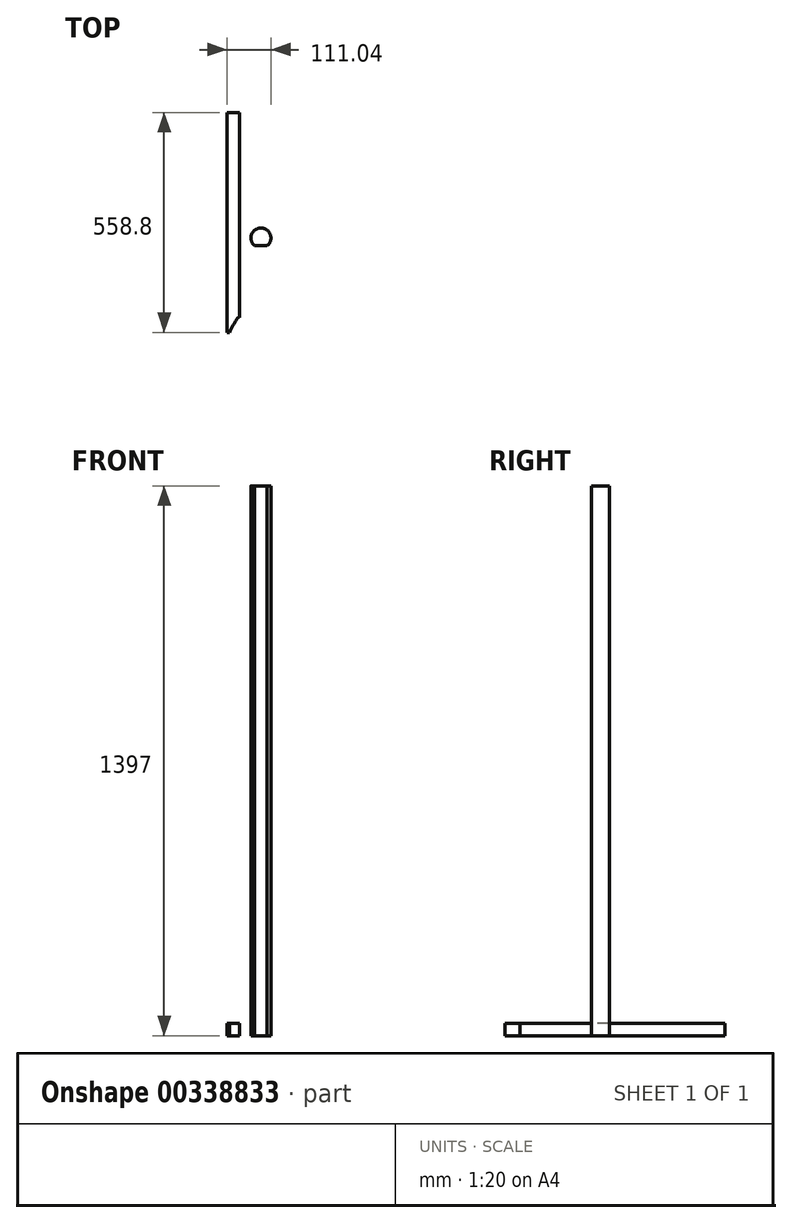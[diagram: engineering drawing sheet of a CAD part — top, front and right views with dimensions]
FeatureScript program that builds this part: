
annotation { "Feature Type Name" : "Feature", "Feature Type Description" : "" }
export const myFeature = defineFeature(function(context is Context, id is Id, definition is map)
    precondition{}
    {
        {
            var Q0;
            Q0=qCreatedBy(makeId("Top.planeOp"),FACE);
            var sketch = newSketch(context, id + "F0", { "sketchPlane" : qUnion([Q0])});
            skLineSegment(sketch, "E0.bottom", {"start": v(-53.31, 332.32) * mm, "end": v(-21.56, 332.32) * mm});
            skLineSegment(sketch, "E0.top", {"start": v(-53.31, -226.48) * mm, "end": v(-21.56, -226.48) * mm});
            skLineSegment(sketch, "E0.left", {"start": v(-53.31, 332.32) * mm, "end": v(-53.31, -226.48) * mm});
            skLineSegment(sketch, "E0.right", {"start": v(-21.56, 332.32) * mm, "end": v(-21.56, -226.48) * mm});
            skLineSegment(sketch, "E1.bottom", {"start": v(-53.31, -226.48) * mm, "end": v(-46.96, -226.48) * mm});
            skLineSegment(sketch, "E1.left", {"start": v(-53.31, -226.48) * mm, "end": v(-53.31, -124.88) * mm});
            skFitSpline(sketch, "E2", {"points": [v(-46.96, -226.48) * mm, v(-21.56, -188.45) * mm, v(-21.56, -200.45) * mm], "startDerivative": vector(40.89, 97.49) * mm, "endDerivative": vector(-1.45, 5.6) * mm});
            skCircle(sketch, "E3", {"center": v(32.33, 13.1) * mm, "radius": 25.4 * mm});
            skLineSegment(sketch, "E4.bottom", {"start": v(16.45, -6.72) * mm, "end": v(48.2, -6.72) * mm});
            skLineSegment(sketch, "E4.top", {"start": v(16.45, -26.61) * mm, "end": v(48.2, -26.61) * mm});
            skLineSegment(sketch, "E4.left", {"start": v(16.45, -6.72) * mm, "end": v(16.45, -26.61) * mm});
            skLineSegment(sketch, "E4.right", {"start": v(48.2, -6.72) * mm, "end": v(48.2, -26.61) * mm});
            skSolve(sketch);
        }
        {
            var Q0;
            {var subQ2=sQuery(id+"F0.wireOp",EDGE,"E0.bottom");Q0=makeQuery(id+"F0.imprint","IMPRINT",FACE,{"disambiguationData":[TD([[makeQuery(id+"F0.imprint","IMPRINT",EDGE,{"derivedFrom":subQ2}),-1.0]])]});}
            extrude(context, id + "F1", {"entities" : qUnion([Q0]), "depth" : 31.75 * mm});
        }
        {
            var Q0;
            {var subQ0=sQuery(id+"F0.wireOp",EDGE,"E4.bottom");Q0=makeQuery(id+"F0.imprint","IMPRINT",FACE,{"disambiguationData":[TD([[makeQuery(id+"F0.imprint","IMPRINT",EDGE,{"derivedFrom":subQ0}),1.0]])]});}
            extrude(context, id + "F2", {"entities" : qUnion([Q0]), "depth" : 1397 * mm});
        }
    });
